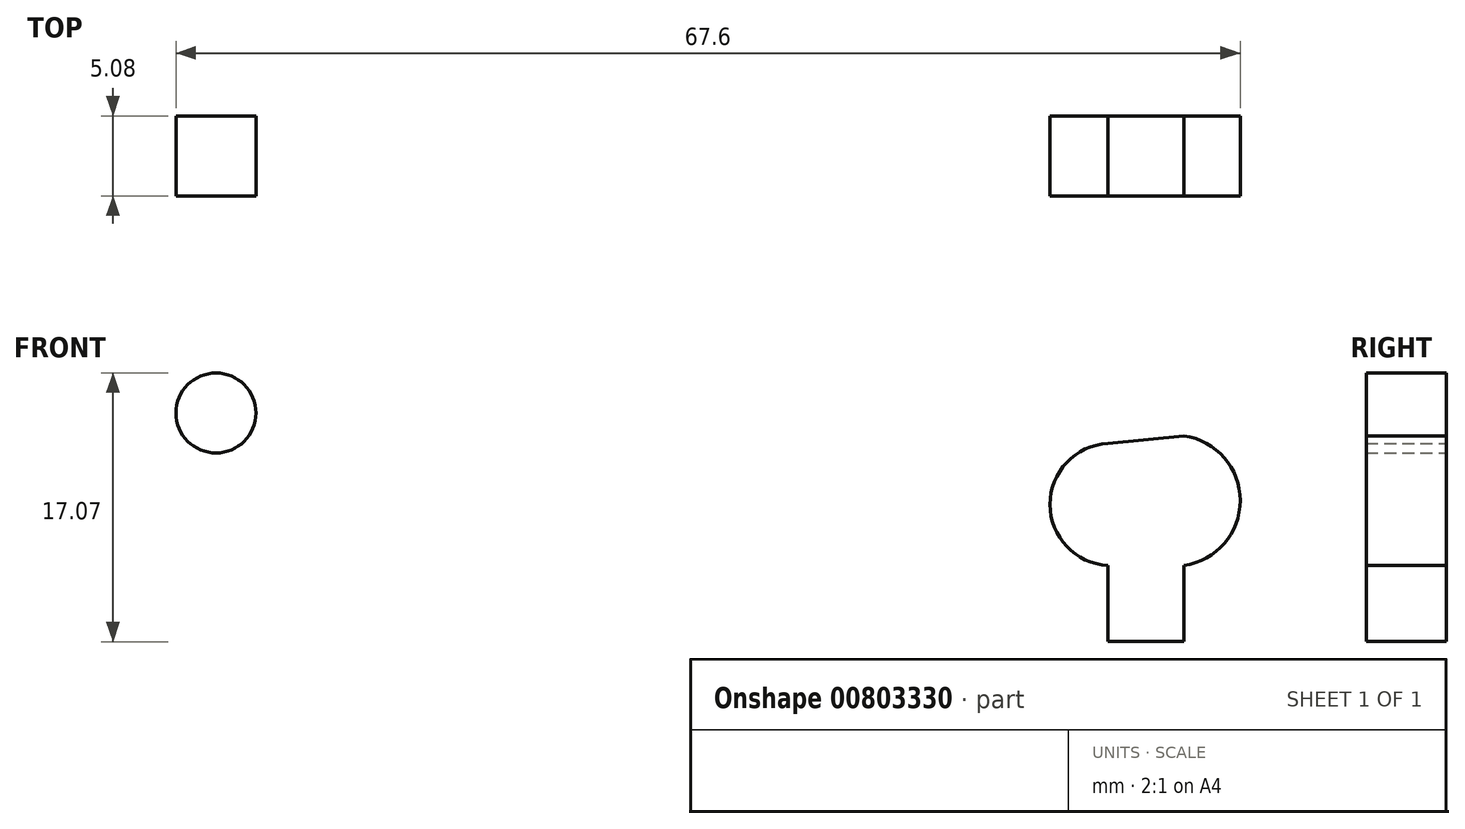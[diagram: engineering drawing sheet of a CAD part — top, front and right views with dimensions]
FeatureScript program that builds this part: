
annotation { "Feature Type Name" : "Feature", "Feature Type Description" : "" }
export const myFeature = defineFeature(function(context is Context, id is Id, definition is map)
    precondition{}
    {
        {
            var Q0;
            Q0=qCreatedBy(makeId("Front.planeOp"),FACE);
            var sketch = newSketch(context, id + "F0", { "sketchPlane" : qUnion([Q0])});
            skCircle(sketch, "E0", {"center": v(-24.45, 23) * mm, "radius": 2.54 * mm});
            skSolve(sketch);
        }
        {
            var Q0;
            Q0 = qSketchRegion(id + "F0", true);
            extrude(context, id + "F1", {"entities" : qUnion([Q0]), "depth" : 5.08 * mm, "offsetDistance" : 25.4 * mm});
        }
        {
            var Q0;
            Q0=qCreatedBy(makeId("Front.planeOp"),FACE);
            var sketch = newSketch(context, id + "F2", { "sketchPlane" : qUnion([Q0])});
            skLineSegment(sketch, "E1", {"start": v(37.04, 13.31) * mm, "end": v(37.04, 8.47) * mm});
            skLineSegment(sketch, "E2", {"start": v(37.04, 8.47) * mm, "end": v(32.2, 8.47) * mm});
            skLineSegment(sketch, "E3", {"start": v(32.2, 8.47) * mm, "end": v(32.2, 13.31) * mm});
            skArc(sketch, "E4", {"start": v(32.2, 21.06) * mm, "mid": v(28.52, 17.19) * mm, "end": v(32.2, 13.31) * mm});
            skArc(sketch, "E5", {"start": v(37.04, 13.31) * mm, "mid": v(40.6, 17.43) * mm, "end": v(37.04, 21.54) * mm});
            skLineSegment(sketch, "E6", {"start": v(32.2, 21.06) * mm, "end": v(37.04, 21.54) * mm});
            skSolve(sketch);
        }
        {
            var Q0;
            Q0 = qSketchRegion(id + "F2", true);
            extrude(context, id + "F3", {"entities" : qUnion([Q0]), "depth" : 5.08 * mm, "offsetDistance" : 25.4 * mm});
        }
    });
